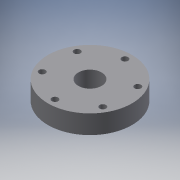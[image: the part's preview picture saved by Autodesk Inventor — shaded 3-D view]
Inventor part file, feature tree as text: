
AUTODESK INVENTOR PART (.ipt)
format: ipt  version: 2016 (Build 200138000, 138)  size: 130,560 bytes
history: native  units: in
note: dims shown in document units (in); Inventor stores cm internally (conversion verified against a paired STEP export)
features: extrude x1, sketch x1
ambient origin geometry x8: Origin, YZ Plane, XZ Plane, XY Plane, X Axis, Y Axis, Z Axis, Center Point
bodies: Body1 (feature_tree)
feature tree (2):
  extrude  "Extrusion2"  Depth=0.503in
  sketch  "Sketch1"  dims[d0=1.875in d1=0.17in d2=0.17in d3=0.17in d4=0.17in d5=0.17in d6=0.17in d7=2.25in d10=0.625in d11=0.503in d12=0.0in]
